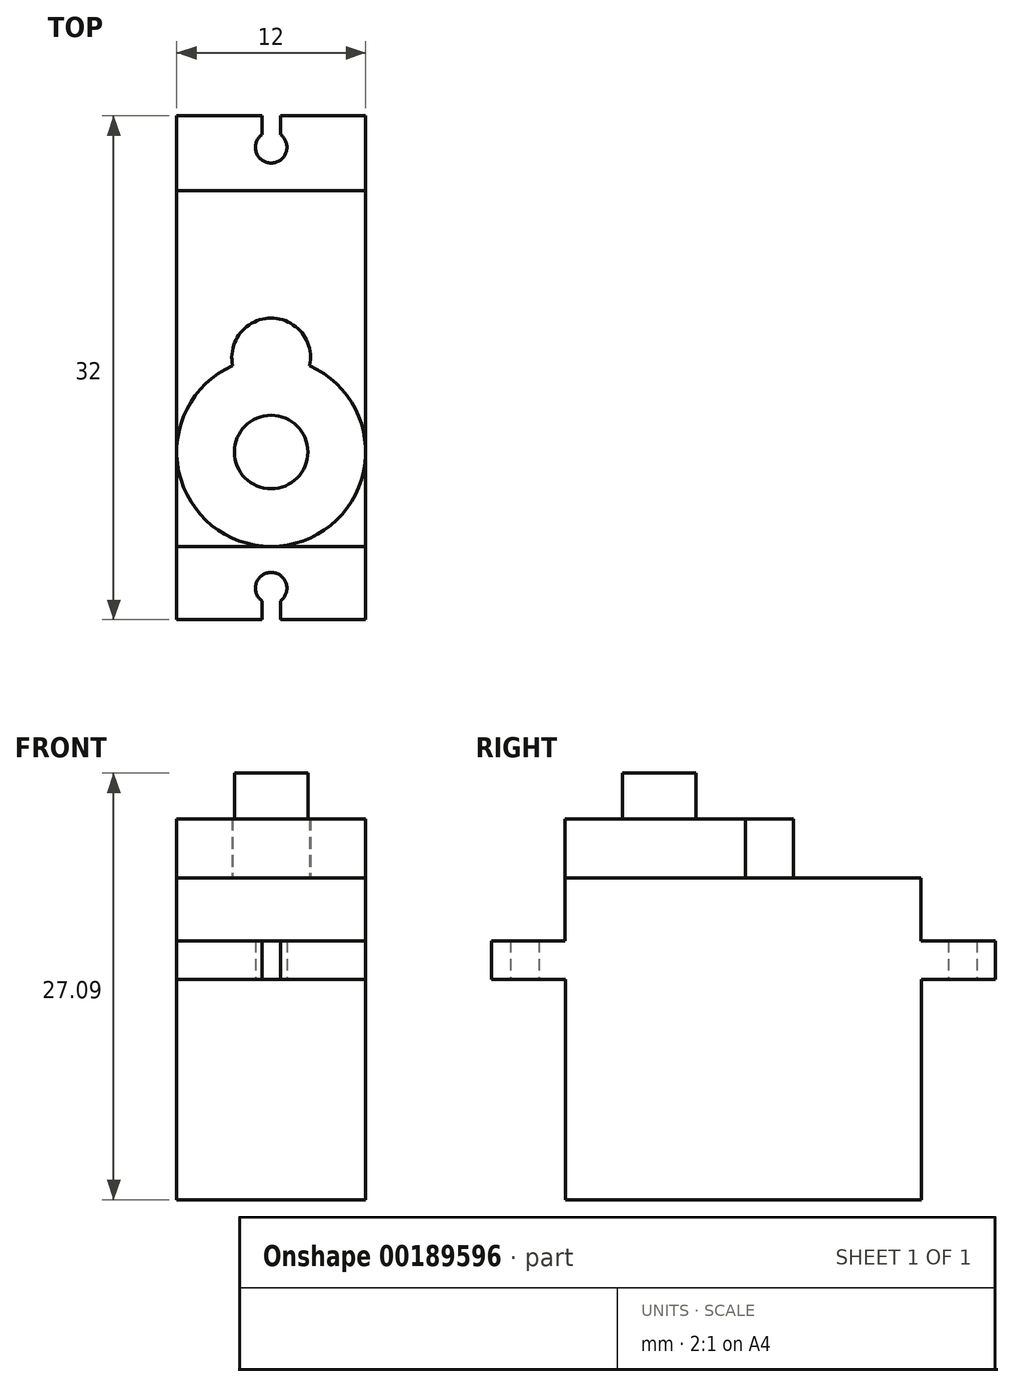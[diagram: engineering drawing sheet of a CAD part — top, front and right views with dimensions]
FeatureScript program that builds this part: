
annotation { "Feature Type Name" : "Feature", "Feature Type Description" : "" }
export const myFeature = defineFeature(function(context is Context, id is Id, definition is map)
    precondition{}
    {
        {
            var Q0;
            Q0=qCreatedBy(makeId("Top.planeOp"),FACE);
            var sketch = newSketch(context, id + "F0", { "sketchPlane" : qUnion([Q0])});
            skLineSegment(sketch, "E0.bottom", {"start": v(7.44, -10.99) * mm, "end": v(19.44, -10.99) * mm});
            skLineSegment(sketch, "E0.top", {"start": v(7.44, -33.59) * mm, "end": v(19.44, -33.59) * mm});
            skLineSegment(sketch, "E0.left", {"start": v(7.44, -10.99) * mm, "end": v(7.44, -33.59) * mm});
            skLineSegment(sketch, "E0.right", {"start": v(19.44, -10.99) * mm, "end": v(19.44, -33.59) * mm});
            skSolve(sketch);
        }
        {
            var Q0;
            Q0 = qSketchRegion(id + "F0", true);
            var Q1;
            Q1=makeQuery(id+"F0.imprint","IMPRINT",FACE,{"disambiguationData":[TD([[makeQuery(id+"F0.imprint","IMPRINT",EDGE,{"derivedFrom":sQuery(id+"F0.wireOp",EDGE,"E0.bottom")}),-1.0]])]});
            var Q2;
            Q2 = qSketchRegion(id + "FOiXTFXalNguIdH_0", true);
            extrude(context, id + "F1", {"entities" : qUnion([Q0, Q1, Q2]), "depth" : 14 * mm});
        }
        {
            var Q0;
            Q0=makeQuery(id+"F1.opExtrude","CAP_FACE",FACE,{"disambiguationData":[OSD([sQuery(id+"F0.wireOp",EDGE,"E0.bottom"),sQuery(id+"F0.wireOp",EDGE,"E0.top"),sQuery(id+"F0.wireOp",EDGE,"E0.left"),sQuery(id+"F0.wireOp",EDGE,"E0.right")])],"isStart":false});
            var sketch = newSketch(context, id + "F2", { "sketchPlane" : qUnion([Q0])});
            skLineSegment(sketch, "E1", {"start": v(19.44, -10.99) * mm, "end": v(19.44, -6.29) * mm});
            skLineSegment(sketch, "E2", {"start": v(19.44, -6.29) * mm, "end": v(7.44, -6.29) * mm});
            skLineSegment(sketch, "E3", {"start": v(7.44, -6.29) * mm, "end": v(7.44, -10.99) * mm});
            skCircle(sketch, "E4", {"center": v(13.44, -8.29) * mm, "radius": 1 * mm});
            skPoint(sketch, "E4.centerSnap0", {"position": v(13.44, -10.99) * mm});
            skLineSegment(sketch, "E5", {"start": v(19.44, -22.29) * mm, "end": v(7.44, -22.29) * mm, "construction": true});
            skLineSegment(sketch, "E6", {"start": v(14.02, -7.48) * mm, "end": v(14.02, -6.29) * mm});
            skLineSegment(sketch, "E7", {"start": v(14.02, -6.29) * mm, "end": v(13.44, -6.29) * mm});
            skLineSegment(sketch, "E8", {"start": v(13.44, -6.29) * mm, "end": v(13.44, -7.29) * mm, "construction": true});
            skLineSegment(sketch, "E9.MirrorCS", {"start": v(12.85, -7.48) * mm, "end": v(12.85, -6.29) * mm});
            skLineSegment(sketch, "E10.MirrorCS", {"start": v(7.44, -38.29) * mm, "end": v(7.44, -33.59) * mm});
            skLineSegment(sketch, "E11.MirrorCS", {"start": v(19.44, -38.29) * mm, "end": v(7.44, -38.29) * mm});
            skLineSegment(sketch, "E12.MirrorCS", {"start": v(19.44, -33.59) * mm, "end": v(19.44, -38.29) * mm});
            skCircle(sketch, "E13.MirrorC", {"center": v(13.44, -36.29) * mm, "radius": 1 * mm});
            skLineSegment(sketch, "E14.MirrorCS", {"start": v(14.02, -37.1) * mm, "end": v(14.02, -38.29) * mm});
            skLineSegment(sketch, "E15.MirrorCS", {"start": v(12.85, -37.1) * mm, "end": v(12.85, -38.29) * mm});
            skSolve(sketch);
        }
        {
            var Q0;
            {var subQ3=sQuery(id+"F2.wireOp",EDGE,"E1");Q0=makeQuery(id+"F2.imprint","IMPRINT",FACE,{"disambiguationData":[TD([[makeQuery(id+"F2.imprint","IMPRINT",EDGE,{"derivedFrom":subQ3}),1.0]])]});}
            var Q1;
            {var subQ2=sQuery(id+"F2.wireOp",EDGE,"E10.MirrorCS");Q1=makeQuery(id+"F2.imprint","IMPRINT",FACE,{"disambiguationData":[TD([[makeQuery(id+"F2.imprint","IMPRINT",EDGE,{"derivedFrom":subQ2}),-1.0]])]});}
            var Q2;
            Q2=makeQuery(id+"F2.imprint","IMPRINT",FACE,{"disambiguationData":[TD([[makeQuery(id+"F2.imprint","IMPRINT",EDGE,{"derivedFrom":makeQuery(id+"F1.opExtrude","CAP_EDGE",EDGE,{"disambiguationData":[OSD([sQuery(id+"F0.wireOp",EDGE,"E0.bottom")])],"isStart":false})}),-1.0]])]});
            extrude(context, id + "F3", {"entities" : qUnion([Q0, Q1, Q2]), "operationType" : NewBodyOperationType.ADD, "depth" : 2.45 * mm});
        }
        {
            var Q0;
            Q0=makeQuery(id+"F3.opExtrude","CAP_FACE",FACE,{"disambiguationData":[OSD([sQuery(id+"F0.wireOp",EDGE,"E0.left"),sQuery(id+"F0.wireOp",EDGE,"E0.right"),sQuery(id+"F2.wireOp",EDGE,"E1"),sQuery(id+"F2.wireOp",EDGE,"E2"),sQuery(id+"F2.wireOp",EDGE,"E3"),sQuery(id+"F2.wireOp",EDGE,"E4"),sQuery(id+"F2.wireOp",EDGE,"E6"),sQuery(id+"F2.wireOp",EDGE,"E9.MirrorCS"),sQuery(id+"F2.wireOp",EDGE,"E10.MirrorCS"),sQuery(id+"F2.wireOp",EDGE,"E11.MirrorCS"),sQuery(id+"F2.wireOp",EDGE,"E12.MirrorCS"),sQuery(id+"F2.wireOp",EDGE,"E13.MirrorC"),sQuery(id+"F2.wireOp",EDGE,"E14.MirrorCS"),sQuery(id+"F2.wireOp",EDGE,"E15.MirrorCS")])],"isStart":false});
            var sketch = newSketch(context, id + "F4", { "sketchPlane" : qUnion([Q0])});
            skLineSegment(sketch, "E16.bottom", {"start": v(19.44, -33.64) * mm, "end": v(7.44, -33.64) * mm});
            skLineSegment(sketch, "E16.top", {"start": v(19.44, -11.04) * mm, "end": v(7.44, -11.04) * mm});
            skLineSegment(sketch, "E16.left", {"start": v(19.44, -33.64) * mm, "end": v(19.44, -11.04) * mm});
            skLineSegment(sketch, "E16.right", {"start": v(7.44, -33.64) * mm, "end": v(7.44, -11.04) * mm});
            skSolve(sketch);
        }
        {
            var Q0;
            Q0=makeQuery(id+"F4.imprint","IMPRINT",FACE,{"disambiguationData":[TD([[makeQuery(id+"F4.imprint","IMPRINT",EDGE,{"derivedFrom":sQuery(id+"F4.wireOp",EDGE,"E16.bottom")}),-1.0]])]});
            extrude(context, id + "F5", {"entities" : qUnion([Q0]), "operationType" : NewBodyOperationType.ADD, "depth" : 4 * mm});
        }
        {
            var Q0;
            Q0=makeQuery(id+"F5.opExtrude","CAP_FACE",FACE,{"disambiguationData":[OSD([sQuery(id+"F4.wireOp",EDGE,"E16.bottom"),sQuery(id+"F4.wireOp",EDGE,"E16.top"),sQuery(id+"F4.wireOp",EDGE,"E16.left"),sQuery(id+"F4.wireOp",EDGE,"E16.right")])],"isStart":false});
            var sketch = newSketch(context, id + "F6", { "sketchPlane" : qUnion([Q0])});
            skLineSegment(sketch, "E17", {"start": v(13.44, -33.64) * mm, "end": v(13.44, -11.04) * mm, "construction": true});
            skLineSegment(sketch, "E18.0", {"start": v(7.44, -11.04) * mm, "end": v(7.44, -33.64) * mm, "construction": true});
            skLineSegment(sketch, "E19.0", {"start": v(19.44, -33.64) * mm, "end": v(7.44, -33.64) * mm, "construction": true});
            skCircle(sketch, "E20", {"center": v(13.44, -27.64) * mm, "radius": 6 * mm});
            skCircle(sketch, "E21", {"center": v(13.44, -21.64) * mm, "radius": 2.5 * mm});
            skPoint(sketch, "E21.centerSnap0", {"position": v(13.44, -22.34) * mm});
            skSolve(sketch);
        }
        {
            var Q0;
            {var subQ0=sQuery(id+"F6.wireOp",EDGE,"E20");var subQ4=sQuery(id+"F6.wireOp",EDGE,"E21");var subQ6=makeQuery(id+"F6.imprint","INTERSECT",VERTEX,{"disambiguationData":[OD(0.0)],"derivedFrom":[subQ0,subQ4]});Q0=makeQuery(id+"F6.imprint","IMPRINT",FACE,{"disambiguationData":[TD([[makeQuery(id+"F6.imprint","IMPRINT",EDGE,{"disambiguationData":[TD([[subQ6,1.0]])],"derivedFrom":subQ0}),1.0]])]});}
            var Q1;
            {var subQ0=sQuery(id+"F6.wireOp",EDGE,"E21");var subQ1=sQuery(id+"F6.wireOp",EDGE,"E20");var subQ2=makeQuery(id+"F6.imprint","INTERSECT",VERTEX,{"disambiguationData":[OD(0.0)],"derivedFrom":[subQ1,subQ0]});Q1=makeQuery(id+"F6.imprint","IMPRINT",FACE,{"disambiguationData":[TD([[makeQuery(id+"F6.imprint","IMPRINT",EDGE,{"disambiguationData":[TD([[subQ2,-1.0]])],"derivedFrom":subQ1}),1.0]])]});}
            var Q2;
            {var subQ0=sQuery(id+"F6.wireOp",EDGE,"E21");var subQ1=sQuery(id+"F6.wireOp",EDGE,"E20");var subQ2=makeQuery(id+"F6.imprint","INTERSECT",VERTEX,{"disambiguationData":[OD(0.0)],"derivedFrom":[subQ1,subQ0]});Q2=makeQuery(id+"F6.imprint","IMPRINT",FACE,{"disambiguationData":[TD([[makeQuery(id+"F6.imprint","IMPRINT",EDGE,{"disambiguationData":[TD([[subQ2,-1.0]])],"derivedFrom":subQ1}),-1.0]])]});}
            extrude(context, id + "F7", {"entities" : qUnion([Q0, Q1, Q2]), "operationType" : NewBodyOperationType.ADD, "depth" : 3.74 * mm});
        }
        {
            var Q0;
            Q0=makeQuery(id+"F7.opExtrude","CAP_FACE",FACE,{"disambiguationData":[OSD([sQuery(id+"F6.wireOp",EDGE,"E20"),sQuery(id+"F6.wireOp",EDGE,"E21")])],"isStart":false});
            var sketch = newSketch(context, id + "F8", { "sketchPlane" : qUnion([Q0])});
            skCircle(sketch, "E22", {"center": v(13.44, -27.64) * mm, "radius": 2.33 * mm});
            skSolve(sketch);
        }
        {
            var Q0;
            Q0=makeQuery(id+"F8.imprint","IMPRINT",FACE,{"disambiguationData":[TD([[makeQuery(id+"F8.imprint","IMPRINT",EDGE,{"derivedFrom":sQuery(id+"F8.wireOp",EDGE,"E22")}),1.0]])]});
            extrude(context, id + "F9", {"entities" : qUnion([Q0]), "operationType" : NewBodyOperationType.ADD, "depth" : 2.9 * mm});
        }
    });
